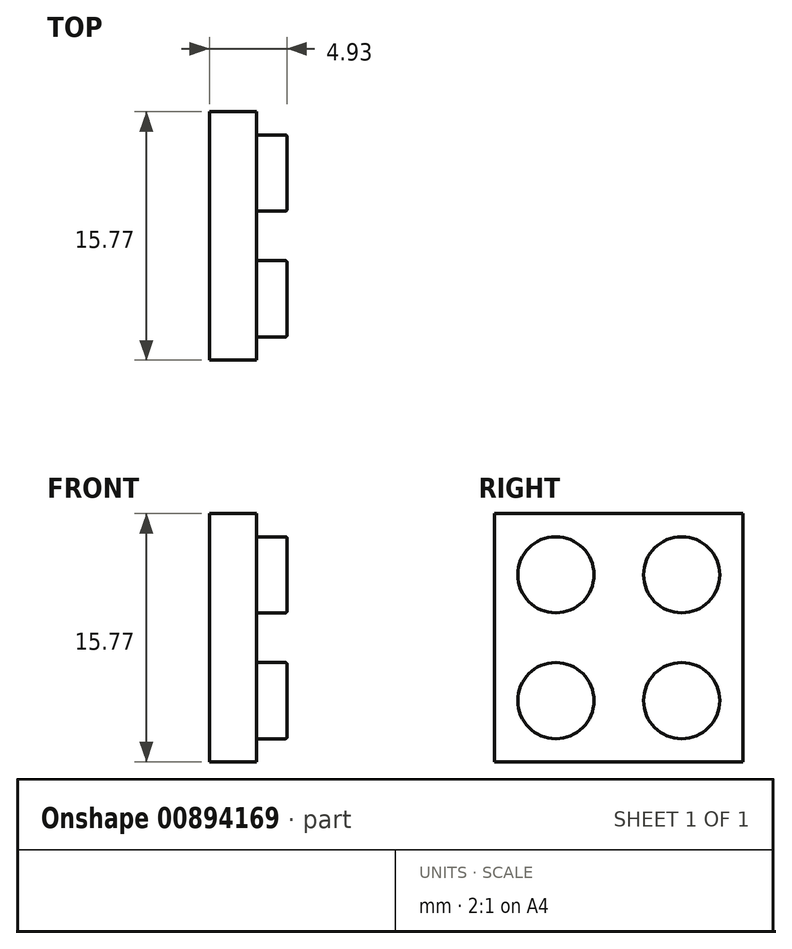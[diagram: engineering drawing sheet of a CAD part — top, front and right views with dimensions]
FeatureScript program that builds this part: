
annotation { "Feature Type Name" : "Feature", "Feature Type Description" : "" }
export const myFeature = defineFeature(function(context is Context, id is Id, definition is map)
    precondition{}
    {
        {
            var Q0;
            Q0=qCreatedBy(makeId("Right.planeOp"),FACE);
            var sketch = newSketch(context, id + "F0", { "sketchPlane" : qUnion([Q0])});
            skLineSegment(sketch, "E0.bottom", {"start": v(-62.98, 64.88) * mm, "end": v(-47.21, 64.88) * mm});
            skLineSegment(sketch, "E0.top", {"start": v(-62.98, 49.1) * mm, "end": v(-47.21, 49.1) * mm});
            skLineSegment(sketch, "E0.left", {"start": v(-62.98, 64.88) * mm, "end": v(-62.98, 49.1) * mm});
            skLineSegment(sketch, "E0.right", {"start": v(-47.21, 64.88) * mm, "end": v(-47.21, 49.1) * mm});
            skCircle(sketch, "E1", {"center": v(-59.1, 60.99) * mm, "radius": 2.42 * mm});
            skCircle(sketch, "E2", {"center": v(-59.1, 53) * mm, "radius": 2.42 * mm});
            skCircle(sketch, "E3", {"center": v(-51.1, 60.99) * mm, "radius": 2.42 * mm});
            skCircle(sketch, "E4", {"center": v(-51.1, 53) * mm, "radius": 2.42 * mm});
            skLineSegment(sketch, "E5.bottom", {"start": v(-51.1, 60.99) * mm, "end": v(-59.1, 60.99) * mm, "construction": true});
            skLineSegment(sketch, "E5.top", {"start": v(-51.1, 53) * mm, "end": v(-59.1, 53) * mm, "construction": true});
            skLineSegment(sketch, "E5.left", {"start": v(-51.1, 60.99) * mm, "end": v(-51.1, 53) * mm, "construction": true});
            skLineSegment(sketch, "E5.right", {"start": v(-59.1, 60.99) * mm, "end": v(-59.1, 53) * mm, "construction": true});
            skLineSegment(sketch, "E6", {"start": v(-62.98, 64.88) * mm, "end": v(-47.21, 49.1) * mm, "construction": true});
            skLineSegment(sketch, "E7", {"start": v(-47.21, 64.88) * mm, "end": v(-62.98, 49.1) * mm, "construction": true});
            skLineSegment(sketch, "E8", {"start": v(-59.1, 63.4) * mm, "end": v(-51.1, 63.4) * mm, "construction": true});
            skLineSegment(sketch, "E9", {"start": v(-51.1, 50.58) * mm, "end": v(-59.1, 50.58) * mm, "construction": true});
            skSolve(sketch);
        }
        {
            var Q0;
            Q0=makeQuery(id+"F0.imprint","IMPRINT",FACE,{"disambiguationData":[TD([[makeQuery(id+"F0.imprint","IMPRINT",EDGE,{"derivedFrom":sQuery(id+"F0.wireOp",EDGE,"E1")}),1.0]])]});
            var Q1;
            Q1=makeQuery(id+"F0.imprint","IMPRINT",FACE,{"disambiguationData":[TD([[makeQuery(id+"F0.imprint","IMPRINT",EDGE,{"derivedFrom":sQuery(id+"F0.wireOp",EDGE,"E3")}),1.0]])]});
            var Q2;
            Q2=makeQuery(id+"F0.imprint","IMPRINT",FACE,{"disambiguationData":[TD([[makeQuery(id+"F0.imprint","IMPRINT",EDGE,{"derivedFrom":sQuery(id+"F0.wireOp",EDGE,"E2")}),1.0]])]});
            var Q3;
            Q3=makeQuery(id+"F0.imprint","IMPRINT",FACE,{"disambiguationData":[TD([[makeQuery(id+"F0.imprint","IMPRINT",EDGE,{"derivedFrom":sQuery(id+"F0.wireOp",EDGE,"E4")}),1.0]])]});
            extrude(context, id + "F1", {"entities" : qUnion([Q0, Q1, Q2, Q3]), "depth" : 1.92 * mm, "offsetDistance" : 25 * mm});
        }
        {
            var Q0;
            Q0=makeQuery(id+"F0.imprint","IMPRINT",FACE,{"disambiguationData":[TD([[makeQuery(id+"F0.imprint","IMPRINT",EDGE,{"derivedFrom":sQuery(id+"F0.wireOp",EDGE,"E0.bottom")}),-1.0]])]});
            var Q1;
            Q1=makeQuery(id+"F0.imprint","IMPRINT",FACE,{"disambiguationData":[TD([[makeQuery(id+"F0.imprint","IMPRINT",EDGE,{"derivedFrom":sQuery(id+"F0.wireOp",EDGE,"E1")}),1.0]])]});
            var Q2;
            Q2=makeQuery(id+"F0.imprint","IMPRINT",FACE,{"disambiguationData":[TD([[makeQuery(id+"F0.imprint","IMPRINT",EDGE,{"derivedFrom":sQuery(id+"F0.wireOp",EDGE,"E3")}),1.0]])]});
            var Q3;
            Q3=makeQuery(id+"F0.imprint","IMPRINT",FACE,{"disambiguationData":[TD([[makeQuery(id+"F0.imprint","IMPRINT",EDGE,{"derivedFrom":sQuery(id+"F0.wireOp",EDGE,"E4")}),1.0]])]});
            var Q4;
            Q4=makeQuery(id+"F0.imprint","IMPRINT",FACE,{"disambiguationData":[TD([[makeQuery(id+"F0.imprint","IMPRINT",EDGE,{"derivedFrom":sQuery(id+"F0.wireOp",EDGE,"E2")}),1.0]])]});
            extrude(context, id + "F2", {"entities" : qUnion([Q0, Q1, Q2, Q3, Q4]), "oppositeDirection" : true, "depth" : 3 * mm, "offsetDistance" : 25 * mm});
        }
        {
            var Q0;
            Q0=makeQuery(id+"F1.opExtrude","CAP_FACE",FACE,{"disambiguationData":[OSD([sQuery(id+"F0.wireOp",EDGE,"E3")])],"isStart":false});
            var Q1;
            Q1=makeQuery(id+"F1.opExtrude","CAP_FACE",FACE,{"disambiguationData":[OSD([sQuery(id+"F0.wireOp",EDGE,"E1")])],"isStart":false});
            var Q2;
            Q2=makeQuery(id+"F1.opExtrude","CAP_FACE",FACE,{"disambiguationData":[OSD([sQuery(id+"F0.wireOp",EDGE,"E2")])],"isStart":false});
            var Q3;
            Q3=makeQuery(id+"F1.opExtrude","CAP_FACE",FACE,{"disambiguationData":[OSD([sQuery(id+"F0.wireOp",EDGE,"E4")])],"isStart":false});
            fillet(context, id + "F3", {"entities" : qUnion([Q0, Q1, Q2, Q3]), "radius" : .1 * mm, "tangentPropagation" : true, "allowEdgeOverflow" : false});
        }
    });
